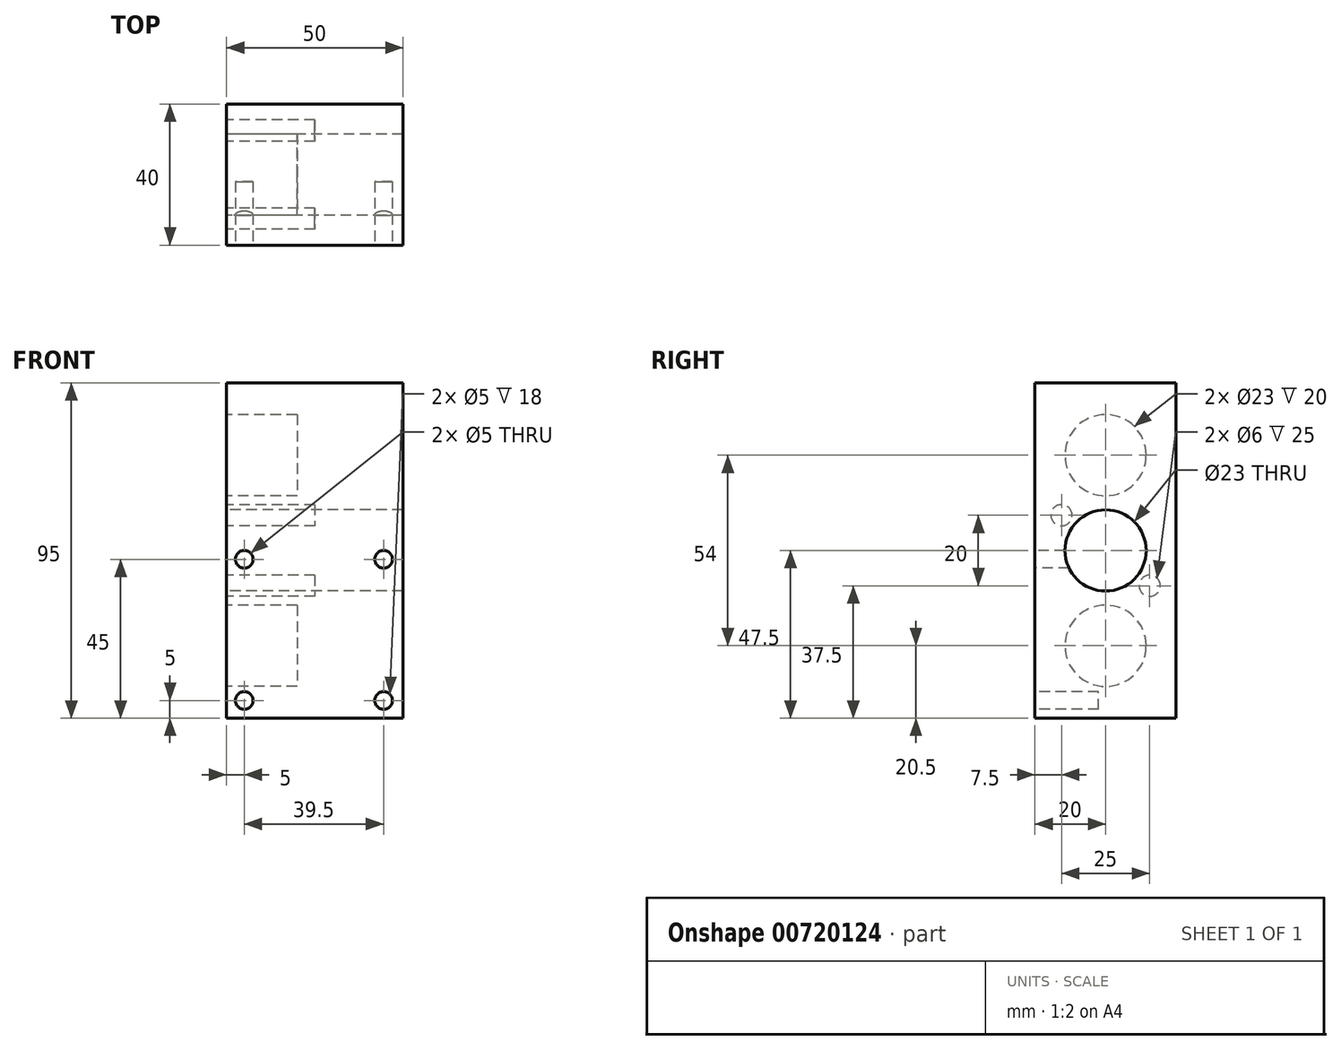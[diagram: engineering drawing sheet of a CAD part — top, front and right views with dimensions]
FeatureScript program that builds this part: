
annotation { "Feature Type Name" : "Feature", "Feature Type Description" : "" }
export const myFeature = defineFeature(function(context is Context, id is Id, definition is map)
    precondition{}
    {
        {
            var Q0;
            Q0=qCreatedBy(makeId("Front.planeOp"),FACE);
            var sketch = newSketch(context, id + "F0", { "sketchPlane" : qUnion([Q0])});
            skLineSegment(sketch, "E0.bottom", {"start": v(0, 0) * mm, "end": v(50, 0) * mm});
            skLineSegment(sketch, "E0.top", {"start": v(0, 95) * mm, "end": v(50, 95) * mm});
            skLineSegment(sketch, "E0.left", {"start": v(0, 0) * mm, "end": v(0, 95) * mm});
            skLineSegment(sketch, "E0.right", {"start": v(50, 0) * mm, "end": v(50, 95) * mm});
            skSolve(sketch);
        }
        {
            var Q0;
            Q0=makeQuery(id+"F0.imprint","IMPRINT",FACE,{"disambiguationData":[TD([[makeQuery(id+"F0.imprint","IMPRINT",EDGE,{"derivedFrom":sQuery(id+"F0.wireOp",EDGE,"E0.bottom")}),1.0]])]});
            extrude(context, id + "F1", {"entities" : qUnion([Q0]), "depth" : 40 * mm, "offsetDistance" : 25 * mm});
        }
        {
            var Q0;
            Q0=makeQuery(id+"F1.opExtrude","CAP_FACE",FACE,{"disambiguationData":[OSD([sQuery(id+"F0.wireOp",EDGE,"E0.bottom"),sQuery(id+"F0.wireOp",EDGE,"E0.top"),sQuery(id+"F0.wireOp",EDGE,"E0.left"),sQuery(id+"F0.wireOp",EDGE,"E0.right")])],"isStart":false});
            var sketch = newSketch(context, id + "F2", { "sketchPlane" : qUnion([Q0])});
            skCircle(sketch, "E1", {"center": v(5, 5) * mm, "radius": 2.5 * mm});
            skCircle(sketch, "E2", {"center": v(44.5, 5) * mm, "radius": 2.5 * mm});
            skCircle(sketch, "E3.0.1.0", {"center": v(5, 45) * mm, "radius": 2.5 * mm});
            skCircle(sketch, "E3.0.1.1", {"center": v(44.5, 45) * mm, "radius": 2.5 * mm});
            skLineSegment(sketch, "E3.direction1", {"start": v(5, 5) * mm, "end": v(30, 5) * mm, "construction": true});
            skLineSegment(sketch, "E3.direction2", {"start": v(5, 5) * mm, "end": v(5, 45) * mm, "construction": true});
            skSolve(sketch);
        }
        {
            var Q0;
            Q0=qSketchRegion(id+"F2",true);
            extrude(context, id + "F3", {"entities" : qUnion([Q0]), "operationType" : NewBodyOperationType.REMOVE, "oppositeDirection" : true, "depth" : 18 * mm, "offsetDistance" : 25 * mm});
        }
        {
            var Q0;
            Q0=makeQuery(id+"F1.opExtrude","SWEPT_FACE",FACE,{"disambiguationData":[OSD([sQuery(id+"F0.wireOp",EDGE,"E0.left")])]});
            var sketch = newSketch(context, id + "F4", { "sketchPlane" : qUnion([Q0])});
            skCircle(sketch, "E4", {"center": v(20, 20.5) * mm, "radius": 11.5 * mm});
            skPoint(sketch, "E4.centerSnap0", {"position": v(20, 0) * mm});
            skCircle(sketch, "E5", {"center": v(20, 74.5) * mm, "radius": 11.5 * mm});
            skSolve(sketch);
        }
        {
            var Q0;
            Q0=makeQuery(id+"F4.imprint","IMPRINT",FACE,{"disambiguationData":[TD([[makeQuery(id+"F4.imprint","IMPRINT",EDGE,{"derivedFrom":sQuery(id+"F4.wireOp",EDGE,"E5")}),1.0]])]});
            var Q1;
            Q1=makeQuery(id+"F4.imprint","IMPRINT",FACE,{"disambiguationData":[TD([[makeQuery(id+"F4.imprint","IMPRINT",EDGE,{"derivedFrom":sQuery(id+"F4.wireOp",EDGE,"E4")}),1.0]])]});
            extrude(context, id + "F5", {"entities" : qUnion([Q0, Q1]), "operationType" : NewBodyOperationType.REMOVE, "oppositeDirection" : true, "depth" : 20 * mm, "offsetDistance" : 25 * mm});
        }
        {
            var Q0;
            Q0=makeQuery(id+"F1.opExtrude","SWEPT_FACE",FACE,{"disambiguationData":[OSD([sQuery(id+"F0.wireOp",EDGE,"E0.left")])]});
            var Q1;
            Q1=makeQuery(id+"F1.opExtrude","SWEPT_FACE",FACE,{"disambiguationData":[OSD([sQuery(id+"F0.wireOp",EDGE,"E0.right")])]});
            cPlane(context, id + "F6", {"entities" : qUnion([Q0, Q1]), "cplaneType" : CPlaneType.MID_PLANE, "offset" : 25 * mm, "width" : 150 * mm, "height" : 150 * mm});
        }
        {
            var Q0;
            Q0=makeQuery(id+"F1.opExtrude","SWEPT_FACE",FACE,{"disambiguationData":[OSD([sQuery(id+"F0.wireOp",EDGE,"E0.left")])]});
            var sketch = newSketch(context, id + "F7", { "sketchPlane" : qUnion([Q0])});
            skCircle(sketch, "E6", {"center": v(20, 47.5) * mm, "radius": 11.5 * mm});
            skPoint(sketch, "E6.centerSnap0", {"position": v(20, 0) * mm});
            skSolve(sketch);
        }
        {
            var Q0;
            Q0=makeQuery(id+"F7.imprint","IMPRINT",FACE,{"disambiguationData":[TD([[makeQuery(id+"F7.imprint","IMPRINT",EDGE,{"derivedFrom":sQuery(id+"F7.wireOp",EDGE,"E6")}),1.0]])]});
            extrude(context, id + "F8", {"entities" : qUnion([Q0]), "operationType" : NewBodyOperationType.REMOVE, "endBound" : BoundingType.THROUGH_ALL, "oppositeDirection" : true, "depth" : 25 * mm, "offsetDistance" : 25 * mm});
        }
        {
            var Q0;
            Q0=makeQuery(id+"F1.opExtrude","SWEPT_FACE",FACE,{"disambiguationData":[OSD([sQuery(id+"F0.wireOp",EDGE,"E0.left")])]});
            var sketch = newSketch(context, id + "F9", { "sketchPlane" : qUnion([Q0])});
            skCircle(sketch, "E7", {"center": v(32.5, 57.5) * mm, "radius": 3 * mm});
            skCircle(sketch, "E8", {"center": v(7.5, 37.5) * mm, "radius": 3 * mm});
            skSolve(sketch);
        }
        {
            var Q0;
            Q0=makeQuery(id+"F9.imprint","IMPRINT",FACE,{"disambiguationData":[TD([[makeQuery(id+"F9.imprint","IMPRINT",EDGE,{"derivedFrom":sQuery(id+"F9.wireOp",EDGE,"E7")}),1.0]])]});
            var Q1;
            Q1=makeQuery(id+"F9.imprint","IMPRINT",FACE,{"disambiguationData":[TD([[makeQuery(id+"F9.imprint","IMPRINT",EDGE,{"derivedFrom":sQuery(id+"F9.wireOp",EDGE,"E8")}),1.0]])]});
            extrude(context, id + "F10", {"entities" : qUnion([Q0, Q1]), "operationType" : NewBodyOperationType.REMOVE, "oppositeDirection" : true, "depth" : 25 * mm, "offsetDistance" : 25 * mm});
        }
    });
